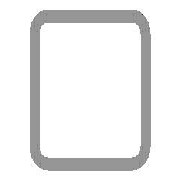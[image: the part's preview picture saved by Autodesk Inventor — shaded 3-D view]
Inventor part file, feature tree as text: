
AUTODESK INVENTOR PART (.ipt)
format: ipt  version: 2018 (Build 220112000, 112)  size: 143,872 bytes
history: native  units: mm (DEFAULTED — no unit token found)
features: other x4, sketch x4, extrude x2, plane x1
ambient origin geometry x8: Origin, YZ Plane, XZ Plane, XY Plane, X Axis, Y Axis, Z Axis, Center Point
bodies: Solid1 (feature_tree)
feature tree (11):
  other  "Piantone tubolare l magg"
  other  "Driven Length"
  other  "Piano iniziale"
  other  "Piano finale"
  extrude  "Corpo"  TaperAngle=0.0deg  [1 undecoded]
  extrude  "Estrusione2"  Depth=40.0mm
  sketch  "Schizzo"
  sketch  "Sketch3"  dims[d3=800.0mm d4=0.0mm]
  plane  "Work Plane3"
  sketch  "Sketch4"  dims[d7=4.0mm d9=40.0mm d11=40.0mm d12=2.0mm d13=-0.0mm d14=800.0mm d15=20.0mm d16=20.0mm d17=90.0deg d18=800.0mm d19=45.0deg d20=10.0mm d21=0.0mm]
  sketch  "Schizzo5"
note: 1 required parameter value undecoded (feature->parameter linkage not recoverable at this tier; creation-order binding heuristic only, values carry confidence <= 0.55)
